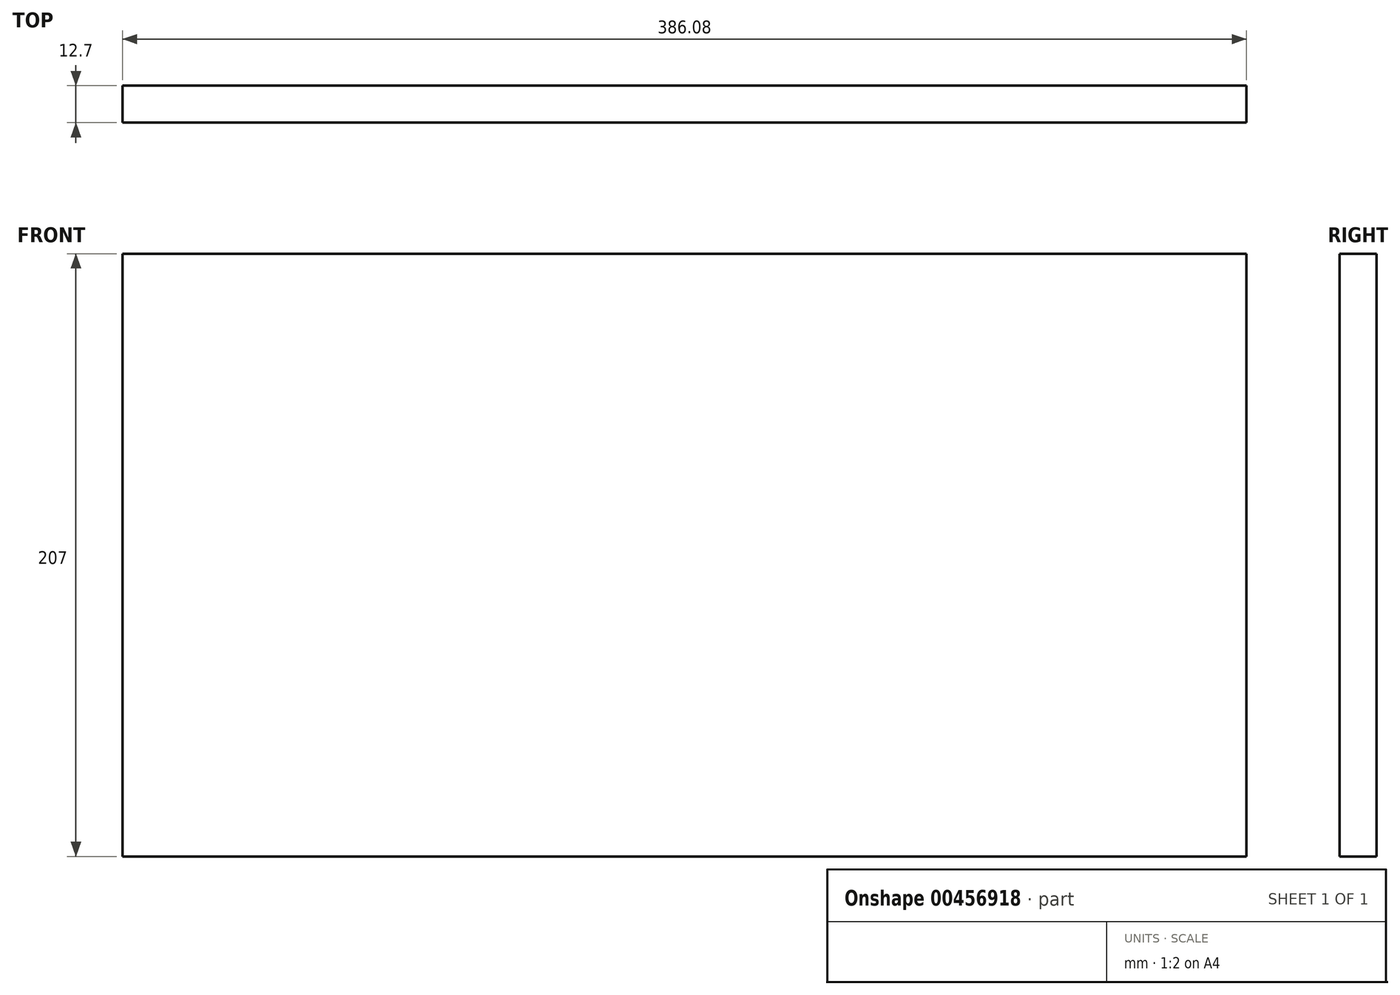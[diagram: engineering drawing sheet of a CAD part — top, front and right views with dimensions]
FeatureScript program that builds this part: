
annotation { "Feature Type Name" : "Feature", "Feature Type Description" : "" }
export const myFeature = defineFeature(function(context is Context, id is Id, definition is map)
    precondition{}
    {
        {
            var Q0;
            Q0=qCreatedBy(makeId("Front.planeOp"),FACE);
            var sketch = newSketch(context, id + "F0", { "sketchPlane" : qUnion([Q0])});
            skLineSegment(sketch, "E0.bottom", {"start": v(-193.04, 103.5) * mm, "end": v(193.04, 103.5) * mm});
            skLineSegment(sketch, "E0.top", {"start": v(-193.04, -103.5) * mm, "end": v(193.04, -103.5) * mm});
            skLineSegment(sketch, "E0.left", {"start": v(-193.04, 103.5) * mm, "end": v(-193.04, -103.5) * mm});
            skLineSegment(sketch, "E0.right", {"start": v(193.04, 103.5) * mm, "end": v(193.04, -103.5) * mm});
            skPoint(sketch, "E0.middle", {"position": v(0, 0) * mm});
            skSolve(sketch);
        }
        {
            var Q0;
            Q0=makeQuery(id+"F0.imprint","IMPRINT",FACE,{"disambiguationData":[TD([[makeQuery(id+"F0.imprint","IMPRINT",EDGE,{"derivedFrom":sQuery(id+"F0.wireOp",EDGE,"E0.bottom")}),-1.0]])]});
            extrude(context, id + "F1", {"entities" : qUnion([Q0]), "depth" : 12.7 * mm});
        }
    });
